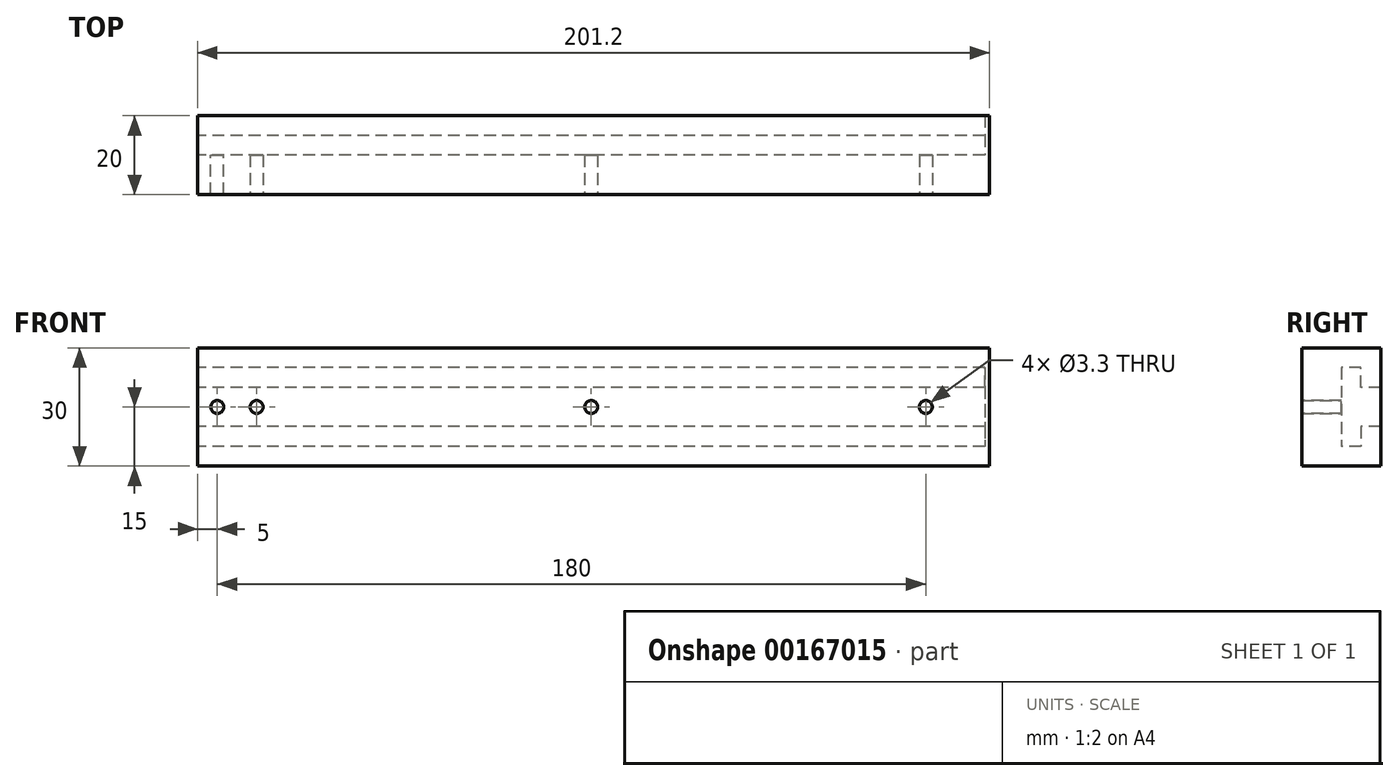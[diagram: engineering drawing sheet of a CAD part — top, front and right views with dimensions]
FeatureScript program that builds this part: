
annotation { "Feature Type Name" : "Feature", "Feature Type Description" : "" }
export const myFeature = defineFeature(function(context is Context, id is Id, definition is map)
    precondition{}
    {
        {
            var Q0;
            Q0=qCreatedBy(makeId("Right.planeOp"),FACE);
            var sketch = newSketch(context, id + "F0", { "sketchPlane" : qUnion([Q0])});
            skLineSegment(sketch, "E0", {"start": v(0, 0) * mm, "end": v(0, 30) * mm});
            skLineSegment(sketch, "E1", {"start": v(0, 30) * mm, "end": v(20, 30) * mm});
            skLineSegment(sketch, "E2", {"start": v(20, 30) * mm, "end": v(20, 25) * mm});
            skLineSegment(sketch, "E3", {"start": v(20, 25) * mm, "end": v(10, 25) * mm});
            skLineSegment(sketch, "E4", {"start": v(0, 15) * mm, "end": v(6.1, 15) * mm});
            skLineSegment(sketch, "E5", {"start": v(10, 25) * mm, "end": v(10, 15) * mm});
            skLineSegment(sketch, "E6.MirrorCS", {"start": v(10, 5) * mm, "end": v(10, 15) * mm});
            skLineSegment(sketch, "E7.MirrorCS", {"start": v(20, 5) * mm, "end": v(10, 5) * mm});
            skLineSegment(sketch, "E8.MirrorCS", {"start": v(20, 0) * mm, "end": v(20, 5) * mm});
            skLineSegment(sketch, "E9.MirrorCS", {"start": v(0, 0) * mm, "end": v(20, 0) * mm});
            skLineSegment(sketch, "E10", {"start": v(10, 15) * mm, "end": v(0, 15) * mm});
            skLineSegment(sketch, "E11", {"start": v(20, 25) * mm, "end": v(20, 20) * mm});
            skLineSegment(sketch, "E12", {"start": v(20, 20) * mm, "end": v(15, 20) * mm});
            skLineSegment(sketch, "E13", {"start": v(15, 20) * mm, "end": v(15, 25) * mm});
            skLineSegment(sketch, "E14.MirrorCS", {"start": v(20, 5) * mm, "end": v(20, 10) * mm});
            skLineSegment(sketch, "E15.MirrorCS", {"start": v(15, 10) * mm, "end": v(15, 5) * mm});
            skLineSegment(sketch, "E16.MirrorCS", {"start": v(20, 10) * mm, "end": v(15, 10) * mm});
            skSolve(sketch);
        }
        {
            var Q0;
            {var subQ3=sQuery(id+"F0.wireOp",EDGE,"E1");Q0=makeQuery(id+"F0.imprint","IMPRINT",FACE,{"disambiguationData":[TD([[makeQuery(id+"F0.imprint","IMPRINT",EDGE,{"derivedFrom":subQ3}),-1.0]])]});}
            var Q1;
            {var subQ0=sQuery(id+"F0.wireOp",EDGE,"E11");Q1=makeQuery(id+"F0.imprint","IMPRINT",FACE,{"disambiguationData":[TD([[makeQuery(id+"F0.imprint","IMPRINT",EDGE,{"derivedFrom":subQ0}),-1.0]])]});}
            var Q2;
            {var subQ0=sQuery(id+"F0.wireOp",EDGE,"E14.MirrorCS");Q2=makeQuery(id+"F0.imprint","IMPRINT",FACE,{"disambiguationData":[TD([[makeQuery(id+"F0.imprint","IMPRINT",EDGE,{"derivedFrom":subQ0}),1.0]])]});}
            var Q3;
            {var subQ1=sQuery(id+"F0.wireOp",EDGE,"E6.MirrorCS");Q3=makeQuery(id+"F0.imprint","IMPRINT",FACE,{"disambiguationData":[TD([[makeQuery(id+"F0.imprint","IMPRINT",EDGE,{"derivedFrom":subQ1}),1.0]])]});}
            extrude(context, id + "F1", {"entities" : qUnion([Q0, Q1, Q2, Q3]), "depth" : 200 * mm});
        }
        {
            var Q0;
            Q0=makeQuery(id+"F1.opExtrude","CAP_FACE",FACE,{"disambiguationData":[OSD([sQuery(id+"F0.wireOp",EDGE,"E0"),sQuery(id+"F0.wireOp",EDGE,"E1"),sQuery(id+"F0.wireOp",EDGE,"E2"),sQuery(id+"F0.wireOp",EDGE,"E3"),sQuery(id+"F0.wireOp",EDGE,"E5"),sQuery(id+"F0.wireOp",EDGE,"E6.MirrorCS"),sQuery(id+"F0.wireOp",EDGE,"E7.MirrorCS"),sQuery(id+"F0.wireOp",EDGE,"E8.MirrorCS"),sQuery(id+"F0.wireOp",EDGE,"E9.MirrorCS"),sQuery(id+"F0.wireOp",EDGE,"E11"),sQuery(id+"F0.wireOp",EDGE,"E12"),sQuery(id+"F0.wireOp",EDGE,"E13"),sQuery(id+"F0.wireOp",EDGE,"E14.MirrorCS"),sQuery(id+"F0.wireOp",EDGE,"E15.MirrorCS"),sQuery(id+"F0.wireOp",EDGE,"E16.MirrorCS")])],"isStart":false});
            var sketch = newSketch(context, id + "F2", { "sketchPlane" : qUnion([Q0])});
            skLineSegment(sketch, "E17", {"start": v(0, 30) * mm, "end": v(20, 30) * mm});
            skLineSegment(sketch, "E18", {"start": v(20, 30) * mm, "end": v(20, 0) * mm});
            skLineSegment(sketch, "E19", {"start": v(20, 0) * mm, "end": v(0, 0) * mm});
            skLineSegment(sketch, "E20", {"start": v(0, 0) * mm, "end": v(0, 30) * mm});
            skSolve(sketch);
        }
        {
            var Q0;
            {var subQ4=sQuery(id+"F2.wireOp",EDGE,"E17");Q0=makeQuery(id+"F2.imprint","IMPRINT",FACE,{"disambiguationData":[TD([[makeQuery(id+"F2.imprint","IMPRINT",EDGE,{"derivedFrom":subQ4}),-1.0]])]});}
            var Q1;
            Q1=makeQuery(id+"F2.imprint","IMPRINT",FACE,{"disambiguationData":[TD([[makeQuery(id+"F2.imprint","IMPRINT",EDGE,{"derivedFrom":makeQuery(id+"F1.opExtrude","CAP_EDGE",EDGE,{"disambiguationData":[OSD([sQuery(id+"F0.wireOp",EDGE,"E3")])],"isStart":false})}),1.0]])]});
            extrude(context, id + "F3", {"entities" : qUnion([Q0, Q1]), "operationType" : NewBodyOperationType.ADD, "depth" : 1.2 * mm});
        }
        {
            var Q0;
            Q0=makeQuery(id+"F1.opExtrude","SWEPT_FACE",FACE,{"disambiguationData":[OSD([sQuery(id+"F0.wireOp",EDGE,"E5"),sQuery(id+"F0.wireOp",EDGE,"E6.MirrorCS")])]});
            var sketch = newSketch(context, id + "F4", { "sketchPlane" : qUnion([Q0])});
            skLineSegment(sketch, "E21", {"start": v(0, 15) * mm, "end": v(-200, 15) * mm});
            skLineSegment(sketch, "E22", {"start": v(-200, 15) * mm, "end": v(-100, 15) * mm});
            skLineSegment(sketch, "E23", {"start": v(-100, 15) * mm, "end": v(-100, 17.07) * mm});
            skLineSegment(sketch, "E24", {"start": v(-200, 15) * mm, "end": v(-185, 15) * mm});
            skLineSegment(sketch, "E25", {"start": v(0, 15) * mm, "end": v(-15, 15) * mm});
            skLineSegment(sketch, "E26", {"start": v(0, 15) * mm, "end": v(-5, 15) * mm});
            skCircle(sketch, "E27", {"center": v(-5, 15) * mm, "radius": 1.65 * mm});
            skSolve(sketch);
        }
        {
            var Q0;
            Q0=qSketchRegion(id+"F4",true);
            extrude(context, id + "F5", {"entities" : qUnion([Q0]), "operationType" : NewBodyOperationType.REMOVE, "oppositeDirection" : true, "depth" : 25 * mm});
        }
        {
            var Q0;
            Q0=sQuery(id+"F4.wireOp",VERTEX,"E25.end");
            var Q1;
            Q1=sQuery(id+"F4.wireOp",VERTEX,"E23.start");
            var Q2;
            Q2=sQuery(id+"F4.wireOp",VERTEX,"E24.end");
            var Q3;
            Q3=makeQuery(id+"F1.opExtrude","SWEPT_BODY",BODY,{"disambiguationData":[OSD([sQuery(id+"F0.wireOp",EDGE,"E0"),sQuery(id+"F0.wireOp",EDGE,"E1"),sQuery(id+"F0.wireOp",EDGE,"E2"),sQuery(id+"F0.wireOp",EDGE,"E3"),sQuery(id+"F0.wireOp",EDGE,"E5"),sQuery(id+"F0.wireOp",EDGE,"E6.MirrorCS"),sQuery(id+"F0.wireOp",EDGE,"E7.MirrorCS"),sQuery(id+"F0.wireOp",EDGE,"E8.MirrorCS"),sQuery(id+"F0.wireOp",EDGE,"E9.MirrorCS"),sQuery(id+"F0.wireOp",EDGE,"E11"),sQuery(id+"F0.wireOp",EDGE,"E12"),sQuery(id+"F0.wireOp",EDGE,"E13"),sQuery(id+"F0.wireOp",EDGE,"E14.MirrorCS"),sQuery(id+"F0.wireOp",EDGE,"E15.MirrorCS"),sQuery(id+"F0.wireOp",EDGE,"E16.MirrorCS")])]});
            hole(context, id + "F6", {"style" : HoleStyle.SIMPLE, "endStyle" : HoleEndStyle.THROUGH, "holeDiameter" : 3.3 * mm, "isTappedThrough" : true, "tappedDepth" : 12 * mm, "tapClearance" : 3, "locations" : qUnion([Q0, Q1, Q2]), "scope" : qUnion([Q3]), "startStyle" : HoleStartStyle.PART});
        }
    });
